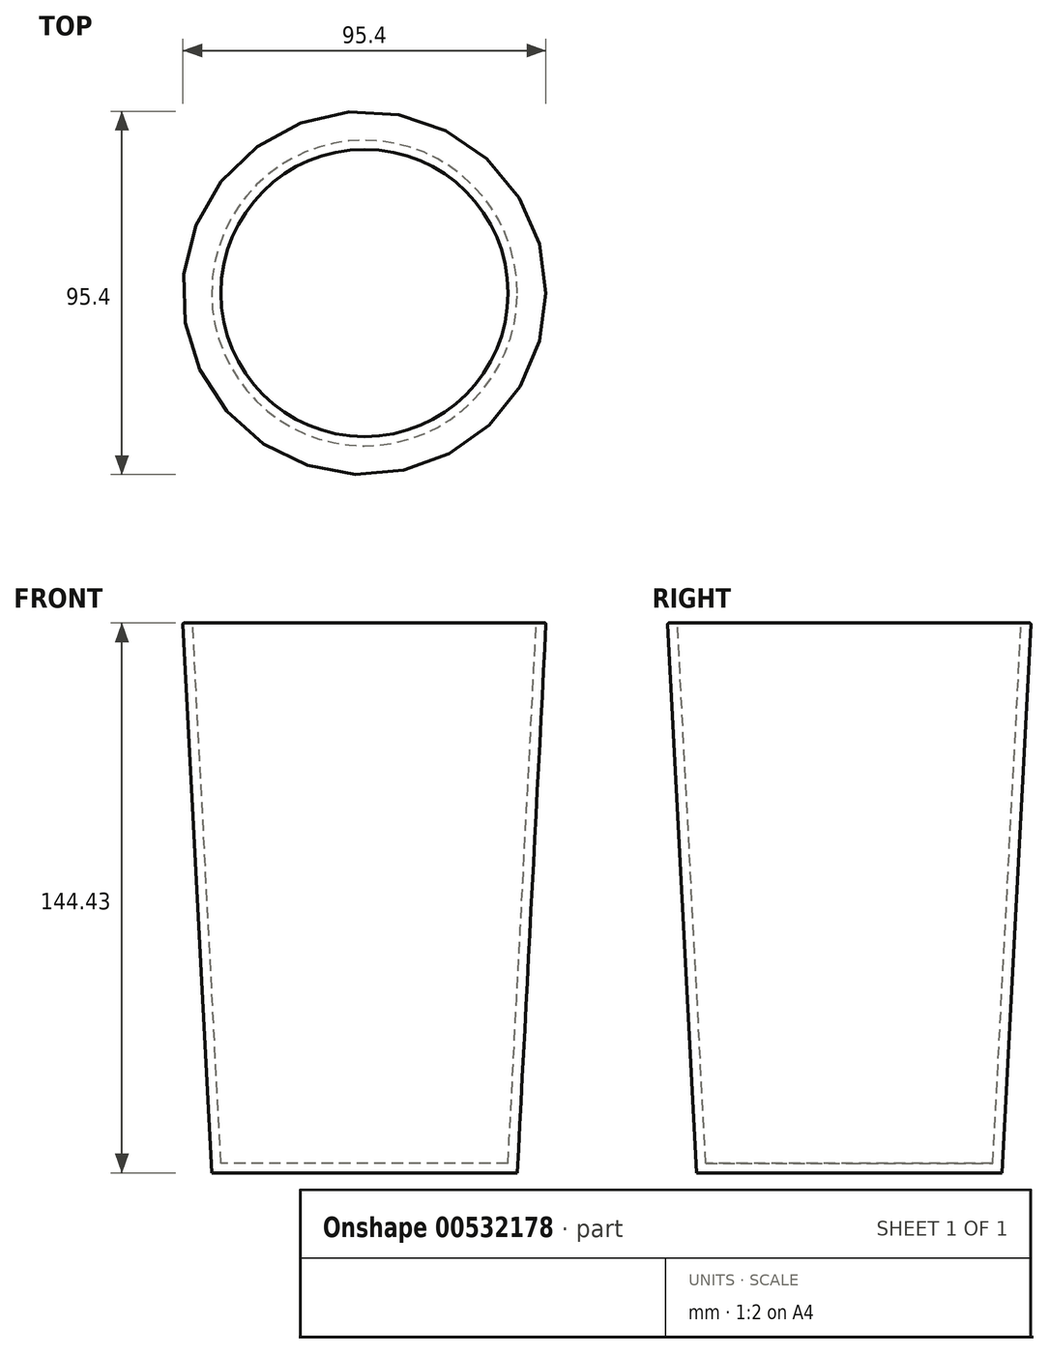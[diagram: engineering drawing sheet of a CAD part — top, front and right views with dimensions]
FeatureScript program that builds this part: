
annotation { "Feature Type Name" : "Feature", "Feature Type Description" : "" }
export const myFeature = defineFeature(function(context is Context, id is Id, definition is map)
    precondition{}
    {
        {
            var Q0;
            Q0=qCreatedBy(makeId("Top.planeOp"),FACE);
            var sketch = newSketch(context, id + "F0", { "sketchPlane" : qUnion([Q0])});
            skCircle(sketch, "E0", {"center": v(0, 0) * mm, "radius": 40.14 * mm});
            skSolve(sketch);
        }
        {
            var Q0;
            Q0=makeQuery(id+"F0.imprint","IMPRINT",FACE,{"disambiguationData":[TD([[makeQuery(id+"F0.imprint","IMPRINT",EDGE,{"derivedFrom":sQuery(id+"F0.wireOp",EDGE,"E0")}),1.0]])]});
            extrude(context, id + "F1", {"entities" : qUnion([Q0]), "depth" : 144.43 * mm, "offsetDistance" : 25.4 * mm, "hasDraft" : true, "draftAngle" : 3 * degree});
        }
        {
            var Q0;
            Q0=makeQuery(id+"F1.opExtrude","CAP_FACE",FACE,{"disambiguationData":[OSD([sQuery(id+"F0.wireOp",EDGE,"E0")])],"isStart":false});
            shell(context, id + "F2", {"entities" : qUnion([Q0]), "thickness" : 2.54 * mm});
        }
        {
            var Q0;
            Q0=makeQuery(id+"F1.opExtrude","CAP_FACE",FACE,{"disambiguationData":[OSD([sQuery(id+"F0.wireOp",EDGE,"E0")])],"isStart":false});
            fillet(context, id + "F3", {"entities" : qUnion([Q0]), "radius" : 0.25 * mm, "allowEdgeOverflow" : false});
        }
    });
